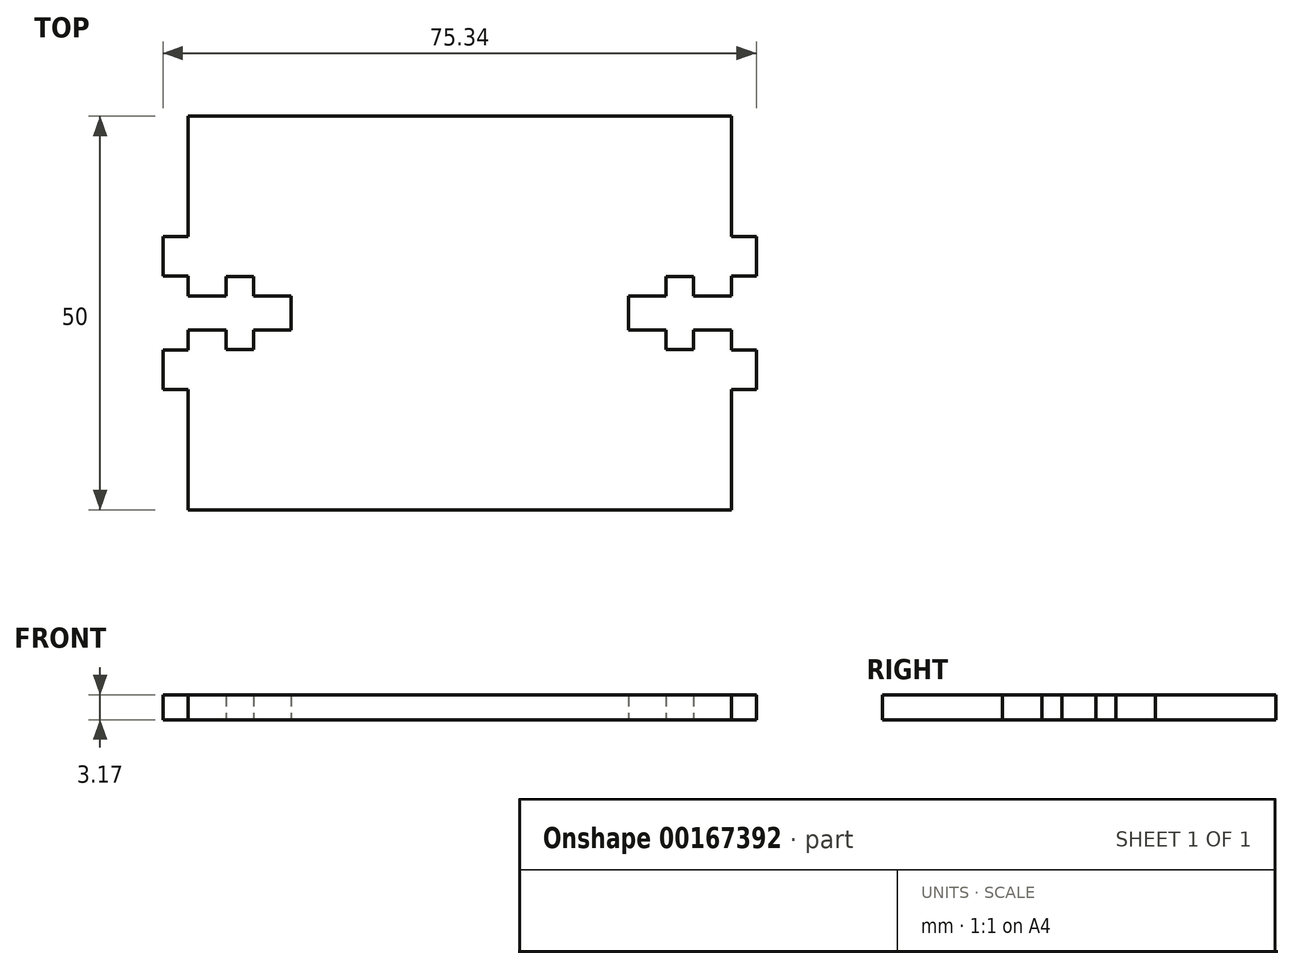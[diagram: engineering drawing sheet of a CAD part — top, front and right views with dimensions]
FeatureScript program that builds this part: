
annotation { "Feature Type Name" : "Feature", "Feature Type Description" : "" }
export const myFeature = defineFeature(function(context is Context, id is Id, definition is map)
    precondition{}
    {
        {
            var Q0;
            Q0=qCreatedBy(makeId("Top.planeOp"),FACE);
            var sketch = newSketch(context, id + "F0", { "sketchPlane" : qUnion([Q0])});
            skLineSegment(sketch, "E0.bottom", {"start": v(-34.5, 25) * mm, "end": v(34.5, 25) * mm});
            skLineSegment(sketch, "E0.top", {"start": v(-34.5, -25) * mm, "end": v(34.5, -25) * mm});
            skPoint(sketch, "E0.middle", {"position": v(0, 0) * mm});
            skLineSegment(sketch, "E1.MirrorCS", {"start": v(26.21, 4.64) * mm, "end": v(26.21, 2.15) * mm});
            skLineSegment(sketch, "E2.MirrorCS", {"start": v(29.7, 4.64) * mm, "end": v(29.7, 2.15) * mm});
            skLineSegment(sketch, "E3.MirrorCS", {"start": v(29.7, -2.15) * mm, "end": v(29.7, -4.64) * mm});
            skLineSegment(sketch, "E4.MirrorCS", {"start": v(26.21, -2.15) * mm, "end": v(26.21, -4.64) * mm});
            skLineSegment(sketch, "E5.MirrorCS", {"start": v(21.44, 2.15) * mm, "end": v(21.44, -2.15) * mm});
            skLineSegment(sketch, "E6.MirrorCS", {"start": v(29.7, -4.64) * mm, "end": v(26.21, -4.64) * mm});
            skLineSegment(sketch, "E7.MirrorCS", {"start": v(21.44, 2.15) * mm, "end": v(26.21, 2.15) * mm});
            skLineSegment(sketch, "E8.MirrorCS", {"start": v(21.44, -2.15) * mm, "end": v(26.21, -2.15) * mm});
            skLineSegment(sketch, "E9.MirrorCS", {"start": v(29.7, 4.64) * mm, "end": v(26.21, 4.64) * mm});
            skLineSegment(sketch, "E10", {"start": v(34.5, -2.15) * mm, "end": v(34.5, -4.7) * mm});
            skLineSegment(sketch, "E11", {"start": v(34.5, -4.7) * mm, "end": v(37.67, -4.7) * mm});
            skLineSegment(sketch, "E12", {"start": v(37.67, -4.7) * mm, "end": v(37.67, -9.7) * mm});
            skLineSegment(sketch, "E13", {"start": v(37.67, -9.7) * mm, "end": v(34.5, -9.7) * mm});
            skLineSegment(sketch, "E14", {"start": v(34.5, -9.7) * mm, "end": v(34.5, -25) * mm});
            skLineSegment(sketch, "E15.MirrorCS", {"start": v(34.5, 9.7) * mm, "end": v(34.5, 25) * mm});
            skLineSegment(sketch, "E16.MirrorCS", {"start": v(37.67, 4.7) * mm, "end": v(37.67, 9.7) * mm});
            skLineSegment(sketch, "E17.MirrorCS", {"start": v(34.5, 2.15) * mm, "end": v(34.5, 4.7) * mm});
            skLineSegment(sketch, "E18.MirrorCS", {"start": v(34.5, 4.7) * mm, "end": v(37.67, 4.7) * mm});
            skLineSegment(sketch, "E19.MirrorCS", {"start": v(37.67, 9.7) * mm, "end": v(34.5, 9.7) * mm});
            skLineSegment(sketch, "E20.MirrorCS", {"start": v(-29.7, 4.64) * mm, "end": v(-26.21, 4.64) * mm});
            skLineSegment(sketch, "E21.MirrorCS", {"start": v(-37.67, -9.7) * mm, "end": v(-34.5, -9.7) * mm});
            skLineSegment(sketch, "E22.MirrorCS", {"start": v(-34.5, 2.15) * mm, "end": v(-34.5, 4.7) * mm});
            skLineSegment(sketch, "E23.MirrorCS", {"start": v(-34.5, -2.15) * mm, "end": v(-34.5, -4.7) * mm});
            skLineSegment(sketch, "E24.MirrorCS", {"start": v(-34.5, 4.7) * mm, "end": v(-37.67, 4.7) * mm});
            skLineSegment(sketch, "E25.MirrorCS", {"start": v(-29.7, 4.64) * mm, "end": v(-29.7, 2.15) * mm});
            skLineSegment(sketch, "E26.MirrorCS", {"start": v(-26.21, 4.64) * mm, "end": v(-26.21, 2.15) * mm});
            skLineSegment(sketch, "E27.MirrorCS", {"start": v(-34.5, -4.7) * mm, "end": v(-37.67, -4.7) * mm});
            skLineSegment(sketch, "E28.MirrorCS", {"start": v(-37.67, 9.7) * mm, "end": v(-34.5, 9.7) * mm});
            skLineSegment(sketch, "E29.MirrorCS", {"start": v(-21.44, 2.15) * mm, "end": v(-21.44, -2.15) * mm});
            skLineSegment(sketch, "E30.MirrorCS", {"start": v(-34.5, -9.7) * mm, "end": v(-34.5, -25) * mm});
            skLineSegment(sketch, "E31.MirrorCS", {"start": v(-21.44, 2.15) * mm, "end": v(-26.21, 2.15) * mm});
            skLineSegment(sketch, "E32.MirrorCS", {"start": v(-34.5, 9.7) * mm, "end": v(-34.5, 25) * mm});
            skLineSegment(sketch, "E33.MirrorCS", {"start": v(-37.67, -4.7) * mm, "end": v(-37.67, -9.7) * mm});
            skLineSegment(sketch, "E34.MirrorCS", {"start": v(-37.67, 4.7) * mm, "end": v(-37.67, 9.7) * mm});
            skLineSegment(sketch, "E35", {"start": v(34.5, 2.15) * mm, "end": v(29.7, 2.15) * mm});
            skLineSegment(sketch, "E36", {"start": v(34.5, -2.15) * mm, "end": v(29.7, -2.15) * mm});
            skLineSegment(sketch, "E37", {"start": v(-34.5, 2.15) * mm, "end": v(-29.7, 2.15) * mm});
            skLineSegment(sketch, "E38.MirrorCS", {"start": v(-21.44, -2.15) * mm, "end": v(-26.21, -2.15) * mm});
            skLineSegment(sketch, "E39.MirrorCS", {"start": v(-26.21, -4.64) * mm, "end": v(-26.21, -2.15) * mm});
            skLineSegment(sketch, "E40.MirrorCS", {"start": v(-29.7, -4.64) * mm, "end": v(-26.21, -4.64) * mm});
            skLineSegment(sketch, "E41.MirrorCS", {"start": v(-29.7, -4.64) * mm, "end": v(-29.7, -2.15) * mm});
            skLineSegment(sketch, "E42.MirrorCS", {"start": v(-34.5, -2.15) * mm, "end": v(-29.7, -2.15) * mm});
            skSolve(sketch);
        }
        {
            var Q0;
            Q0 = qSketchRegion(id + "F0", true);
            extrude(context, id + "F1", {"entities" : qUnion([Q0]), "depth" : 3.17 * mm});
        }
    });
